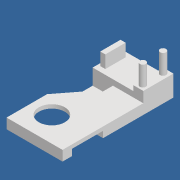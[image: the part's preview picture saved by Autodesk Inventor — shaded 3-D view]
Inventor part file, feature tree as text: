
AUTODESK INVENTOR PART (.ipt)
format: ipt  version: 2020 (Build 240168000, 168)  size: 218,112 bytes
history: native  units: mm
features: extrude x13, sketch x13, other x2, chamfer x1, loft x1, projected_geometry x1
ambient origin geometry x8: Origin, YZ Plane, XZ Plane, XY Plane, X Axis, Y Axis, Z Axis, Center Point
bodies: Solid1 (feature_tree)
feature tree (31):
  extrude  "Extrusion1"  Depth=23.8mm
  extrude  "Extrusion2"  Depth=16.0mm
  extrude  "Extrusion3"  Depth=8.0mm TaperAngle=0.0deg
  chamfer  "Chamfer1"  Distance=5.0mm
  extrude  "Extrusion4"  Depth=16.0mm
  extrude  "Extrusion5"  Depth=32.0mm TaperAngle=0.0deg
  extrude  "Extrusion6"  Depth=7.6mm
  sketch  "Sketch9"  dims[d13=8.0mm d14=2.0mm d15=45.0deg d18=16.0mm]
  extrude  "Extrusion7"  Depth=31.8mm TaperAngle=0.0deg
  extrude  "Extrusion8"  Depth=4.7mm
  extrude  "Extrusion9"  Depth=19.8mm
  extrude  "Extrusion10"  Depth=23.8mm
  extrude  "Extrusion11"  Depth=8.0mm
  extrude  "Extrusion12"  Depth=16.0mm TaperAngle=0.0deg
  loft  "Loft1"
  extrude  "Extrusion13"  Depth=24.0mm TaperAngle=0.0deg
  sketch  "Sketch1"  dims[d0=24.0mm d1=23.8mm]
  sketch  "Sketch3"  dims[d2=8.0mm d3=0.0mm d4=16.0mm]
  sketch  "Sketch4"  dims[d5=3.0mm d6=8.0mm d7=0.0mm]
  sketch  "Sketch6"  dims[d8=4.7mm]
  sketch  "Sketch7"  dims[d9=4.3mm]
  sketch  "Sketch8"  dims[d10=4.0mm d11=5.0mm d12=0.0mm]
  sketch  "Sketch10"  dims[d19=3.0mm d20=32.0mm d21=0.0mm]
  sketch  "Sketch11"  dims[d22=16.0mm d23=7.6mm]
  sketch  "Sketch12"  dims[d24=5.0mm d25=0.0mm d26=31.8mm d27=0.0mm]
  sketch  "Sketch13"  dims[d28=4.7mm d29=4.7mm]
  projected_geometry  "Projected Loop1"
  sketch  "Sketch14"  dims[d30=16.0mm d32=19.8mm]
  other  "Edges1"
  other  "Edges2"
  sketch  "Sketch15"  dims[d33=11.8mm d34=23.8mm d35=8.0mm d36=16.0mm d37=0.0mm d38=4.4mm d39=0.0mm d40=24.0mm d41=0.0mm d42=8.0mm d43=23.8mm d44=4.0mm d45=0.0mm d46=28.2mm d47=0.0mm d48=20.5mm d49=16.0mm d51=19.8mm d52=3.0mm d53=0.0mm d54=0.0mm d55=90.0deg d56=0.0mm d57=90.0deg d58=4.0mm d59=16.0mm d60=4.0mm d61=2.0mm d62=10.0mm d63=0.0mm]
